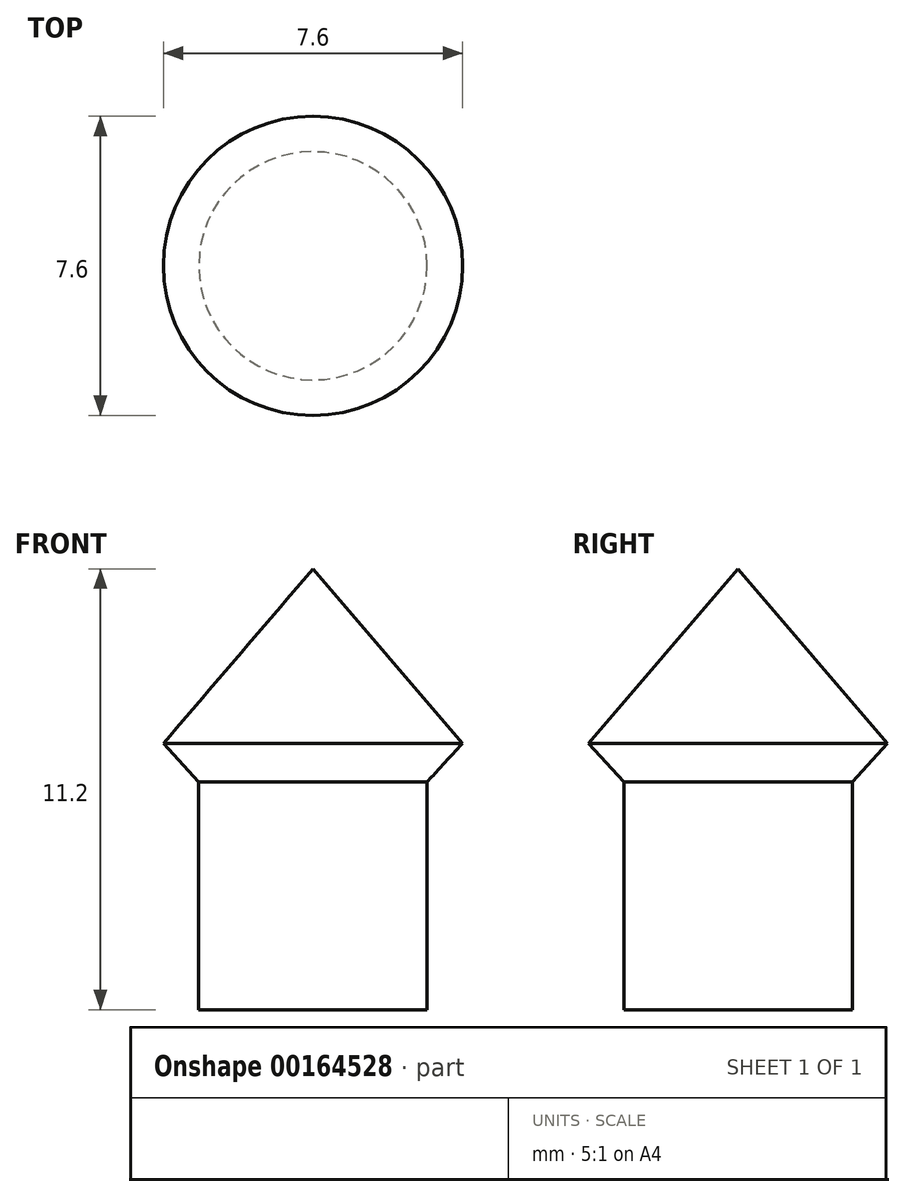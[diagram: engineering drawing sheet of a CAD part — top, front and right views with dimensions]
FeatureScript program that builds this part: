
annotation { "Feature Type Name" : "Feature", "Feature Type Description" : "" }
export const myFeature = defineFeature(function(context is Context, id is Id, definition is map)
    precondition{}
    {
        {
            var Q0;
            Q0=qCreatedBy(makeId("Top.planeOp"),FACE);
            var sketch = newSketch(context, id + "F0", { "sketchPlane" : qUnion([Q0])});
            skCircle(sketch, "E0", {"center": v(0, 0) * mm, "radius": 2.9 * mm});
            skSolve(sketch);
        }
        {
            var Q0;
            Q0 = qSketchRegion(id + "F0", true);
            extrude(context, id + "F1", {"entities" : qUnion([Q0]), "depth" : 7 * mm});
        }
        {
            var Q0;
            Q0=qCreatedBy(makeId("Front.planeOp"),FACE);
            var sketch = newSketch(context, id + "F2", { "sketchPlane" : qUnion([Q0])});
            skLineSegment(sketch, "E1", {"start": v(0, 6.77) * mm, "end": v(0, 11.2) * mm});
            skLineSegment(sketch, "E2", {"start": v(0, 11.2) * mm, "end": v(-3.8, 6.77) * mm});
            skLineSegment(sketch, "E3", {"start": v(-3.8, 6.77) * mm, "end": v(0, 6.77) * mm});
            skLineSegment(sketch, "E4", {"start": v(-3.8, 6.77) * mm, "end": v(0, 2.62) * mm});
            skLineSegment(sketch, "E5", {"start": v(0, 2.62) * mm, "end": v(0, 6.77) * mm});
            skSolve(sketch);
        }
        {
            var Q0;
            Q0 = qSketchRegion(id + "F2", true);
            var Q1;
            Q1=sQuery(id+"F2.wireOp",EDGE,"E1");
            revolve(context, id + "F3", {"operationType" : NewBodyOperationType.ADD, "entities" : qUnion([Q0]), "axis" : qUnion([Q1]), "revolveType" : RevolveType.FULL});
        }
    });
